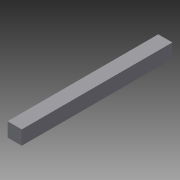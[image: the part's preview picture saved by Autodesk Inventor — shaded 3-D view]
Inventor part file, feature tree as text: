
AUTODESK INVENTOR PART (.ipt)
format: ipt  version: 2015 (Build 190159000, 159)  size: 78,848 bytes
history: native  units: in
note: dims shown in document units (in); Inventor stores cm internally (conversion verified against a paired STEP export)
features: extrude x2, sketch x2, projected_geometry x1
ambient origin geometry x8: Origin, YZ Plane, XZ Plane, XY Plane, X Axis, Y Axis, Z Axis, Center Point
bodies: Solid1 (feature_tree)
feature tree (5):
  extrude  "Extrusion1"  Depth=0.75in
  extrude  "Extrusion2"  Depth=8.0in
  sketch  "Sketch1"  dims[d0=0.75in d1=0.75in]
  sketch  "Sketch2"  dims[d2=8.0in d3=0.0in d4=0.25in d5=8.0in d6=0.0in]
  projected_geometry  "Projected Loop1"
